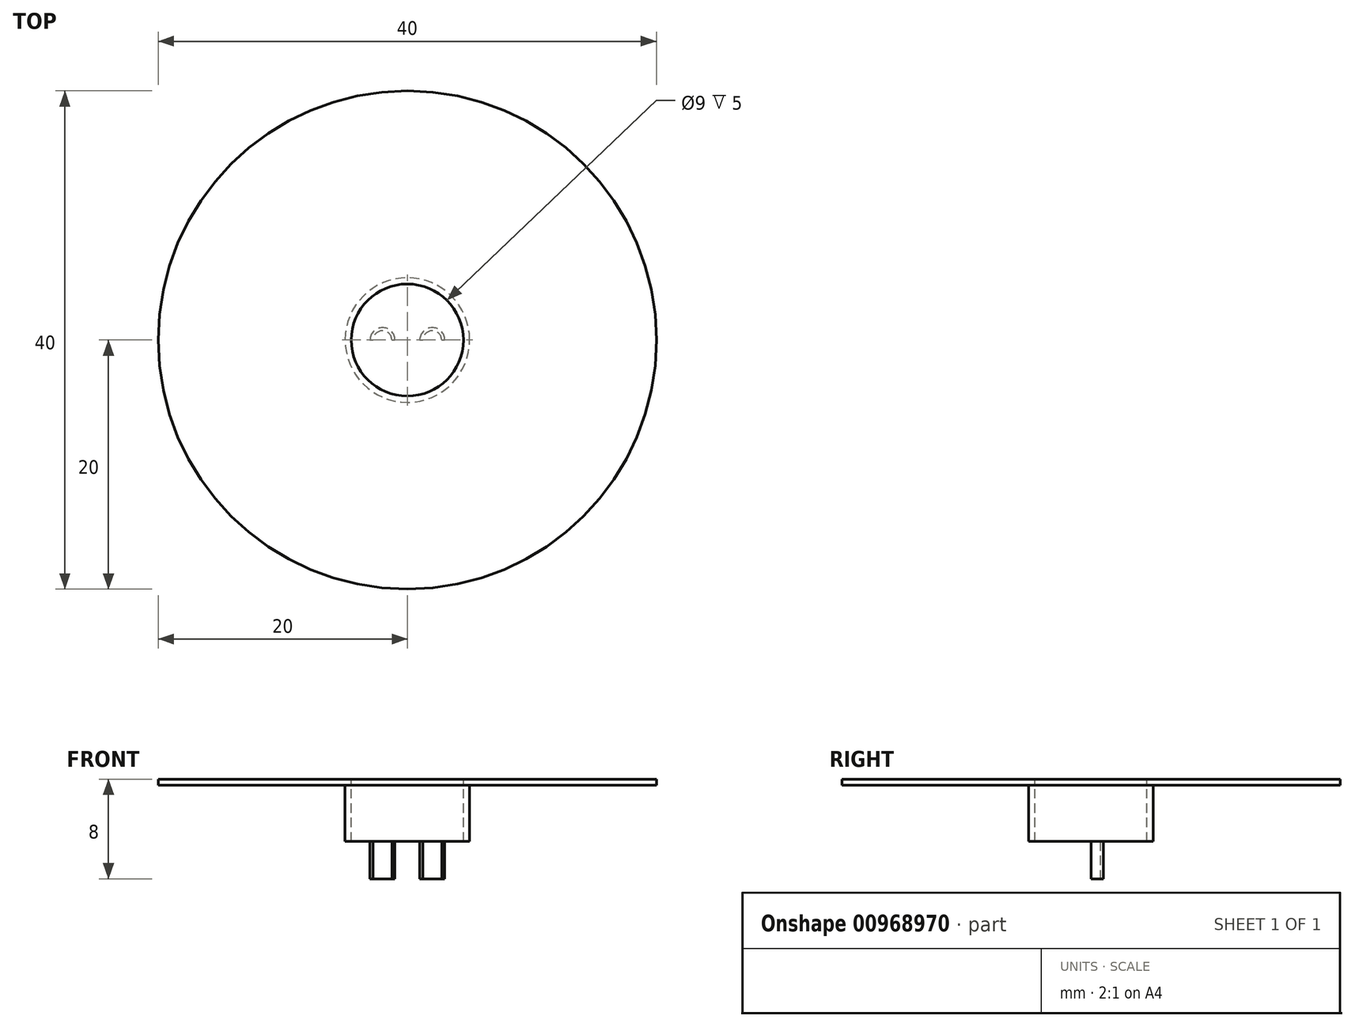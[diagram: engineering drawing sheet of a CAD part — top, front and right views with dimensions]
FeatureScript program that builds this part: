
annotation { "Feature Type Name" : "Feature", "Feature Type Description" : "" }
export const myFeature = defineFeature(function(context is Context, id is Id, definition is map)
    precondition{}
    {
        {
            var Q0;
            Q0=qCreatedBy(makeId("Top.planeOp"),FACE);
            var sketch = newSketch(context, id + "F0", { "sketchPlane" : qUnion([Q0])});
            skCircle(sketch, "E0", {"center": v(0, 0) * mm, "radius": 20 * mm});
            skSolve(sketch);
        }
        {
            var Q0;
            Q0=qSketchRegion(id+"F0",true);
            extrude(context, id + "F1", {"entities" : qUnion([Q0]), "depth" : 0.5 * mm, "offsetDistance" : 25 * mm});
        }
        {
            var Q0;
            Q0=makeQuery(id+"F1.opExtrude","CAP_FACE",FACE,{"disambiguationData":[OSD([sQuery(id+"F0.wireOp",EDGE,"E0")])],"isStart":false});
            var sketch = newSketch(context, id + "F2", { "sketchPlane" : qUnion([Q0])});
            skCircle(sketch, "E1", {"center": v(0, 0) * mm, "radius": 5 * mm});
            skSolve(sketch);
        }
        {
            var Q0;
            Q0=qSketchRegion(id+"F2",true);
            extrude(context, id + "F3", {"entities" : qUnion([Q0]), "operationType" : NewBodyOperationType.ADD, "oppositeDirection" : true, "depth" : 5 * mm, "offsetDistance" : 25 * mm});
        }
        {
            var Q0;
            Q0=makeQuery(id+"F1.opExtrude","CAP_FACE",FACE,{"disambiguationData":[OSD([sQuery(id+"F0.wireOp",EDGE,"E0")])],"isStart":false});
            var sketch = newSketch(context, id + "F4", { "sketchPlane" : qUnion([Q0])});
            skCircle(sketch, "E2", {"center": v(0, 0) * mm, "radius": 4.5 * mm});
            skSolve(sketch);
        }
        {
            var Q0;
            Q0=qSketchRegion(id+"F4",true);
            extrude(context, id + "F5", {"entities" : qUnion([Q0]), "operationType" : NewBodyOperationType.REMOVE, "oppositeDirection" : true, "depth" : 25 * mm, "offsetDistance" : 25 * mm});
        }
        {
            var Q0;
            Q0=makeQuery(id+"F1.opExtrude","CAP_FACE",FACE,{"disambiguationData":[OSD([sQuery(id+"F0.wireOp",EDGE,"E0")])],"isStart":false});
            var sketch = newSketch(context, id + "F6", { "sketchPlane" : qUnion([Q0])});
            skCircle(sketch, "E3", {"center": v(0, 0) * mm, "radius": 4.5 * mm});
            skSolve(sketch);
        }
        {
            var Q0;
            Q0=qSketchRegion(id+"F6",true);
            extrude(context, id + "F7", {"entities" : qUnion([Q0]), "oppositeDirection" : true, "depth" : 5 * mm, "offsetDistance" : 25 * mm});
        }
        {
            var Q0;
            Q0=makeQuery(id+"F7.opExtrude","CAP_FACE",FACE,{"disambiguationData":[OSD([sQuery(id+"F6.wireOp",EDGE,"E3")])],"isStart":true});
            var sketch = newSketch(context, id + "F8", { "sketchPlane" : qUnion([Q0])});
            skCircle(sketch, "E4", {"center": v(-2, 0) * mm, "radius": 1 * mm});
            skCircle(sketch, "E5", {"center": v(2, 0) * mm, "radius": 1 * mm});
            skSolve(sketch);
        }
        {
            var Q0;
            Q0=qSketchRegion(id+"F8",true);
            extrude(context, id + "F9", {"entities" : qUnion([Q0]), "operationType" : NewBodyOperationType.ADD, "oppositeDirection" : true, "depth" : 8 * mm, "offsetDistance" : 25 * mm});
        }
        {
            var Q0;
            Q0=makeQuery(id+"F9.opExtrude","CAP_FACE",FACE,{"disambiguationData":[OSD([sQuery(id+"F8.wireOp",EDGE,"E4")])],"isStart":false});
            var sketch = newSketch(context, id + "F10", { "sketchPlane" : qUnion([Q0])});
            skArc(sketch, "E6", {"start": v(-1, 0) * mm, "mid": v(-2, 1) * mm, "end": v(-3, 0) * mm});
            skArc(sketch, "E7", {"start": v(-2.75, 0) * mm, "mid": v(-2, -0.75) * mm, "end": v(-1.25, 0) * mm});
            skLineSegment(sketch, "E8", {"start": v(-3, 0) * mm, "end": v(-2.75, 0) * mm});
            skLineSegment(sketch, "E9", {"start": v(-1.25, 0) * mm, "end": v(-1, 0) * mm});
            skArc(sketch, "E10.1.0.0", {"start": v(3, 0) * mm, "mid": v(2, 1) * mm, "end": v(1, 0) * mm});
            skLineSegment(sketch, "E10.1.0.1", {"start": v(1, 0) * mm, "end": v(1.25, 0) * mm});
            skLineSegment(sketch, "E10.1.0.2", {"start": v(2.75, 0) * mm, "end": v(3, 0) * mm});
            skArc(sketch, "E10.1.0.3", {"start": v(1.25, 0) * mm, "mid": v(2, -0.75) * mm, "end": v(2.75, 0) * mm});
            skLineSegment(sketch, "E10.direction1", {"start": v(-3, 0) * mm, "end": v(1, 0) * mm, "construction": true});
            skSolve(sketch);
        }
        {
            var Q0;
            Q0=qSketchRegion(id+"F10",true);
            extrude(context, id + "F11", {"entities" : qUnion([Q0]), "operationType" : NewBodyOperationType.REMOVE, "oppositeDirection" : true, "depth" : 3 * mm, "offsetDistance" : 25 * mm});
        }
    });
